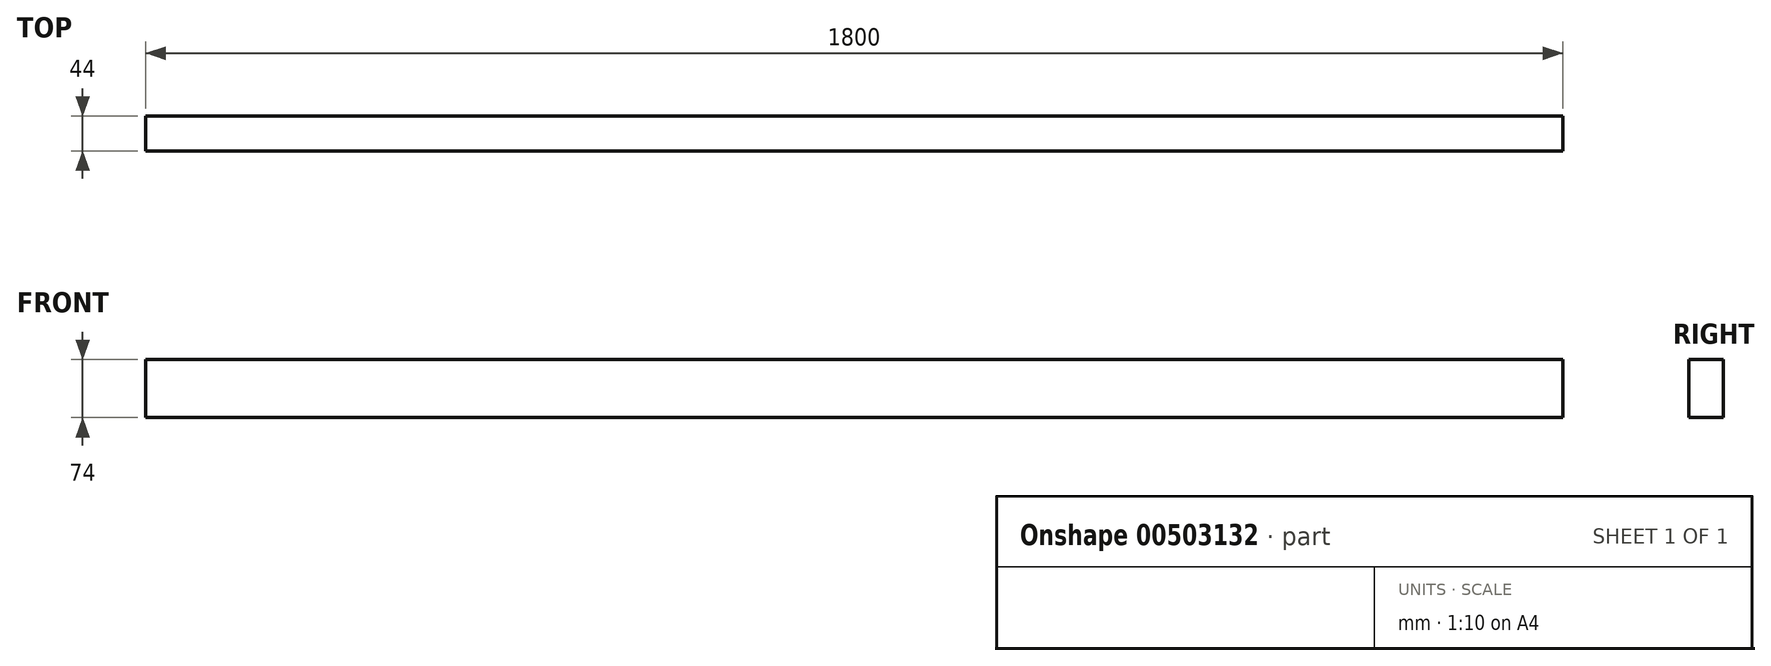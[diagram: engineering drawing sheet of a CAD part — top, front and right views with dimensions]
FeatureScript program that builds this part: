
annotation { "Feature Type Name" : "Feature", "Feature Type Description" : "" }
export const myFeature = defineFeature(function(context is Context, id is Id, definition is map)
    precondition{}
    {
        {
            var Q0;
            Q0=qCreatedBy(makeId("Front.planeOp"),FACE);
            var sketch = newSketch(context, id + "F0", { "sketchPlane" : qUnion([Q0])});
            skLineSegment(sketch, "E0.bottom", {"start": v(-410.5, 34.9) * mm, "end": v(1389.5, 34.9) * mm});
            skLineSegment(sketch, "E0.top", {"start": v(-410.5, -39.1) * mm, "end": v(1389.5, -39.1) * mm});
            skLineSegment(sketch, "E0.left", {"start": v(-410.5, 34.9) * mm, "end": v(-410.5, -39.1) * mm});
            skLineSegment(sketch, "E0.right", {"start": v(1389.5, 34.9) * mm, "end": v(1389.5, -39.1) * mm});
            skSolve(sketch);
        }
        {
            var Q0;
            Q0=makeQuery(id+"F0.imprint","IMPRINT",FACE,{"disambiguationData":[TD([[makeQuery(id+"F0.imprint","IMPRINT",EDGE,{"derivedFrom":sQuery(id+"F0.wireOp",EDGE,"E0.bottom")}),-1.0]])]});
            extrude(context, id + "F1", {"entities" : qUnion([Q0]), "depth" : 44 * mm, "offsetDistance" : 25 * mm});
        }
        {
            var Q0;
            Q0=makeQuery(id+"F1.opExtrude","SWEPT_FACE",FACE,{"disambiguationData":[OSD([sQuery(id+"F0.wireOp",EDGE,"E0.bottom")])]});
            var sketch = newSketch(context, id + "F2", { "sketchPlane" : qUnion([Q0])});
            skLineSegment(sketch, "E1", {"start": v(-290.5, 0) * mm, "end": v(-290.5, -44) * mm, "construction": true});
            skLineSegment(sketch, "E2", {"start": v(1269.5, 0) * mm, "end": v(1269.5, -44) * mm, "construction": true});
            skSolve(sketch);
        }
    });
